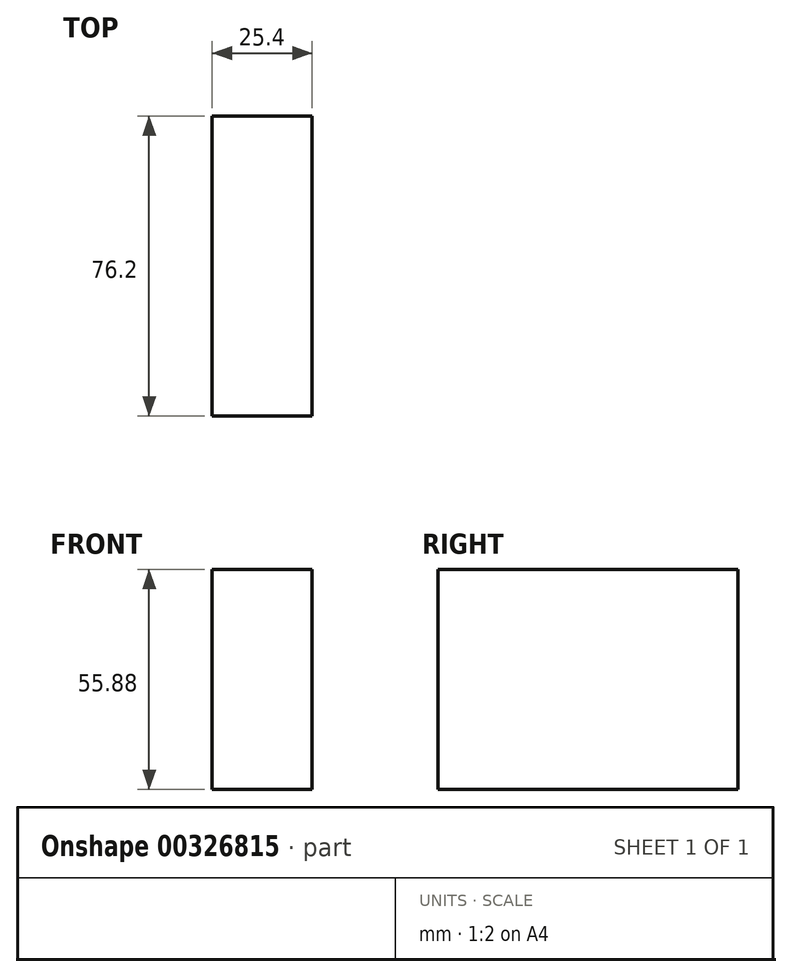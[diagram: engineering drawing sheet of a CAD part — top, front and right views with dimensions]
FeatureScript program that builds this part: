
annotation { "Feature Type Name" : "Feature", "Feature Type Description" : "" }
export const myFeature = defineFeature(function(context is Context, id is Id, definition is map)
    precondition{}
    {
        {
            var Q0;
            Q0=qCreatedBy(makeId("Right.planeOp"),FACE);
            var sketch = newSketch(context, id + "F0", { "sketchPlane" : qUnion([Q0])});
            skLineSegment(sketch, "E0", {"start": v(0, 0) * mm, "end": v(0, 55.88) * mm});
            skLineSegment(sketch, "E1", {"start": v(0, 55.88) * mm, "end": v(-76.2, 55.88) * mm});
            skLineSegment(sketch, "E2", {"start": v(-76.2, 55.88) * mm, "end": v(-76.2, 0) * mm});
            skLineSegment(sketch, "E3", {"start": v(-76.2, 0) * mm, "end": v(0, 0) * mm});
            skSolve(sketch);
        }
        {
            var Q0;
            Q0=makeQuery(id+"F0.imprint","IMPRINT",FACE,{"disambiguationData":[TD([[makeQuery(id+"F0.imprint","IMPRINT",EDGE,{"derivedFrom":sQuery(id+"F0.wireOp",EDGE,"E0")}),1.0]])]});
            extrude(context, id + "F1", {"entities" : qUnion([Q0]), "oppositeDirection" : true, "depth" : 25.4 * mm});
        }
    });
